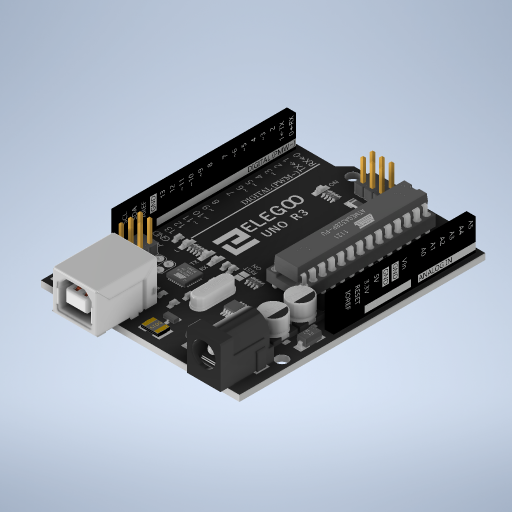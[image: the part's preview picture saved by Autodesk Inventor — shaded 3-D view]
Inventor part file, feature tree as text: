
AUTODESK INVENTOR PART (.ipt)
format: ipt  version: 2024 (Build 280153000, 153)  size: 18,806,272 bytes
history: native  units: in
note: dims shown in document units (in); Inventor stores cm internally (conversion verified against a paired STEP export)
features: other x713, projected_geometry x17, sketch x1
ambient origin geometry x8: Origin, YZ Plane, XZ Plane, XY Plane, X Axis, Y Axis, Z Axis, Center Point
bodies: Solid1 (feature_tree), Solid2 (feature_tree), Solid3 (feature_tree), Solid4 (feature_tree), Solid5 (feature_tree), Solid6 (feature_tree), Solid7 (feature_tree), Solid8 (feature_tree), Solid9 (feature_tree), Solid10 (feature_tree), Solid11 (feature_tree), Solid12 (feature_tree), Solid13 (feature_tree), Solid14 (feature_tree), Solid15 (feature_tree), Solid16 (feature_tree), Solid17 (feature_tree), Solid18 (feature_tree), Solid19 (feature_tree), Solid20 (feature_tree), Solid21 (feature_tree), Solid22 (feature_tree), Solid23 (feature_tree), Solid24 (feature_tree), Solid25 (feature_tree), Solid26 (feature_tree), Solid27 (feature_tree), Solid28 (feature_tree), Solid29 (feature_tree), Solid30 (feature_tree), Solid31 (feature_tree), Solid32 (feature_tree), Solid33 (feature_tree), Solid34 (feature_tree), Solid35 (feature_tree), Solid36 (feature_tree), Solid37 (feature_tree), Solid38 (feature_tree), Solid39 (feature_tree), Solid40 (feature_tree), Solid41 (feature_tree), Solid42 (feature_tree), Solid43 (feature_tree), Solid44 (feature_tree), Solid45 (feature_tree), Solid46 (feature_tree), Solid47 (feature_tree), Solid48 (feature_tree), Solid49 (feature_tree), Solid50 (feature_tree), Solid51 (feature_tree), Solid52 (feature_tree), Solid53 (feature_tree), Solid54 (feature_tree), Solid55 (feature_tree), Solid56 (feature_tree), Solid57 (feature_tree), Solid58 (feature_tree), Solid59 (feature_tree), Solid60 (feature_tree), Solid61 (feature_tree), Solid62 (feature_tree), Solid63 (feature_tree), Solid64 (feature_tree), Solid65 (feature_tree), Solid66 (feature_tree), Solid67 (feature_tree), Solid68 (feature_tree), Solid69 (feature_tree), Solid70 (feature_tree), Solid71 (feature_tree), Solid72 (feature_tree), Solid73 (feature_tree), Solid74 (feature_tree), Solid75 (feature_tree), Solid76 (feature_tree), Solid77 (feature_tree), Solid78 (feature_tree), Solid79 (feature_tree), Solid80 (feature_tree), Solid81 (feature_tree), Solid82 (feature_tree), Solid83 (feature_tree), Solid84 (feature_tree), Solid85 (feature_tree), Solid86 (feature_tree), Solid87 (feature_tree), Solid88 (feature_tree), Solid89 (feature_tree), Solid90 (feature_tree), Solid91 (feature_tree), Solid92 (feature_tree), Solid93 (feature_tree), Solid94 (feature_tree), Solid95 (feature_tree), Solid96 (feature_tree), Solid97 (feature_tree), Solid98 (feature_tree), Solid99 (feature_tree), Solid100 (feature_tree), Solid101 (feature_tree), Solid102 (feature_tree), Solid103 (feature_tree), Solid104 (feature_tree), Solid105 (feature_tree), Solid106 (feature_tree), Solid107 (feature_tree), Solid108 (feature_tree), Solid109 (feature_tree), Solid110 (feature_tree), Solid111 (feature_tree), Solid112 (feature_tree), Solid113 (feature_tree), Solid114 (feature_tree), Solid115 (feature_tree), Solid116 (feature_tree), Solid117 (feature_tree), Solid118 (feature_tree), Solid119 (feature_tree), Solid120 (feature_tree), Solid121 (feature_tree), Solid122 (feature_tree), Solid123 (feature_tree), Solid124 (feature_tree), Solid125 (feature_tree), Solid126 (feature_tree), Solid127 (feature_tree), Solid128 (feature_tree), Solid129 (feature_tree), Solid130 (feature_tree), Solid131 (feature_tree), Solid132 (feature_tree), Solid133 (feature_tree), Solid134 (feature_tree), Solid135 (feature_tree), Solid136 (feature_tree), Solid137 (feature_tree), Solid138 (feature_tree), Solid139 (feature_tree), Solid140 (feature_tree), Solid141 (feature_tree), Solid142 (feature_tree), Solid143 (feature_tree), Solid144 (feature_tree), Solid145 (feature_tree), Solid146 (feature_tree), Solid147 (feature_tree), Solid148 (feature_tree), Solid149 (feature_tree), Solid150 (feature_tree), Solid151 (feature_tree), Solid152 (feature_tree), Solid153 (feature_tree), Solid154 (feature_tree), Solid155 (feature_tree), Solid156 (feature_tree), Solid157 (feature_tree), Solid158 (feature_tree), Solid159 (feature_tree), Solid160 (feature_tree), Solid161 (feature_tree), Solid162 (feature_tree), Solid163 (feature_tree), Solid164 (feature_tree), Solid165 (feature_tree), Solid166 (feature_tree), Solid167 (feature_tree), Solid168 (feature_tree), Solid169 (feature_tree), Solid170 (feature_tree), Solid171 (feature_tree), Solid172 (feature_tree), Solid173 (feature_tree), Solid174 (feature_tree), Solid175 (feature_tree), Solid176 (feature_tree), Solid177 (feature_tree), Solid178 (feature_tree), Solid179 (feature_tree), Solid180 (feature_tree), Solid181 (feature_tree), Solid182 (feature_tree), Solid183 (feature_tree), Solid184 (feature_tree), Solid185 (feature_tree), Solid186 (feature_tree), Solid187 (feature_tree), Solid188 (feature_tree), Solid189 (feature_tree), Solid190 (feature_tree), Solid191 (feature_tree), Solid192 (feature_tree), Solid193 (feature_tree), Solid194 (feature_tree), Solid195 (feature_tree), Solid196 (feature_tree), Solid197 (feature_tree), Solid198 (feature_tree), Solid199 (feature_tree), Solid200 (feature_tree), Solid201 (feature_tree), Solid202 (feature_tree), Solid203 (feature_tree), Solid204 (feature_tree), Solid205 (feature_tree), Solid206 (feature_tree), Solid207 (feature_tree), Solid208 (feature_tree), Solid209 (feature_tree), Solid210 (feature_tree), Solid211 (feature_tree), Solid212 (feature_tree), Solid213 (feature_tree), Solid214 (feature_tree), Solid215 (feature_tree), Solid216 (feature_tree), Solid217 (feature_tree), Solid218 (feature_tree), Solid219 (feature_tree), Solid220 (feature_tree), Solid221 (feature_tree), Solid222 (feature_tree), Solid223 (feature_tree), Solid224 (feature_tree), Solid225 (feature_tree), Solid226 (feature_tree), Solid227 (feature_tree), Solid228 (feature_tree), Solid229 (feature_tree), Solid230 (feature_tree), Solid231 (feature_tree), Solid232 (feature_tree), Solid233 (feature_tree), Solid234 (feature_tree), Solid235 (feature_tree), Solid236 (feature_tree), Solid237 (feature_tree), Solid238 (feature_tree), Solid239 (feature_tree), Solid240 (feature_tree), Solid241 (feature_tree), Solid242 (feature_tree), Solid243 (feature_tree), Solid244 (feature_tree), Solid245 (feature_tree), Solid246 (feature_tree), Solid247 (feature_tree), Solid248 (feature_tree), Solid249 (feature_tree), Solid250 (feature_tree), Solid251 (feature_tree), Solid252 (feature_tree), Solid253 (feature_tree), Solid254 (feature_tree), Solid255 (feature_tree), Solid256 (feature_tree), Solid257 (feature_tree), Solid258 (feature_tree), Solid259 (feature_tree), Solid260 (feature_tree), Solid261 (feature_tree), Solid262 (feature_tree), Solid263 (feature_tree), Solid264 (feature_tree), Solid265 (feature_tree), Solid266 (feature_tree), Solid267 (feature_tree), Solid268 (feature_tree), Solid269 (feature_tree), Solid270 (feature_tree), Solid271 (feature_tree), Solid272 (feature_tree), Solid273 (feature_tree), Solid274 (feature_tree), Solid275 (feature_tree), Solid276 (feature_tree), Solid277 (feature_tree), Solid278 (feature_tree), Solid279 (feature_tree), Solid280 (feature_tree), Solid281 (feature_tree), Solid282 (feature_tree), Solid283 (feature_tree), Solid284 (feature_tree), Solid285 (feature_tree), Solid286 (feature_tree), Solid287 (feature_tree), Solid288 (feature_tree), Solid289 (feature_tree), Solid290 (feature_tree), Solid291 (feature_tree), Solid292 (feature_tree), Solid293 (feature_tree), Solid294 (feature_tree), Solid295 (feature_tree), Solid296 (feature_tree), Solid297 (feature_tree), Solid298 (feature_tree), Solid299 (feature_tree), Solid300 (feature_tree), Solid301 (feature_tree), Solid302 (feature_tree), Solid303 (feature_tree), Solid304 (feature_tree), Solid305 (feature_tree), Solid306 (feature_tree), Solid307 (feature_tree), Solid308 (feature_tree), Solid309 (feature_tree), Solid310 (feature_tree), Solid311 (feature_tree), Solid312 (feature_tree), Solid313 (feature_tree), Solid314 (feature_tree), Solid315 (feature_tree), Solid316 (feature_tree), Solid317 (feature_tree), Solid318 (feature_tree), Solid319 (feature_tree), Solid320 (feature_tree), Solid321 (feature_tree), Solid322 (feature_tree), Solid323 (feature_tree), Solid324 (feature_tree), Solid325 (feature_tree), Solid326 (feature_tree), Solid327 (feature_tree), Solid328 (feature_tree), Solid329 (feature_tree), Solid330 (feature_tree), Solid331 (feature_tree), Solid332 (feature_tree), Solid333 (feature_tree), Solid334 (feature_tree), Solid335 (feature_tree), Solid336 (feature_tree), Solid337 (feature_tree), Solid338 (feature_tree), Solid339 (feature_tree), Solid340 (feature_tree), Solid341 (feature_tree), Solid342 (feature_tree), Solid343 (feature_tree), Solid344 (feature_tree), Solid345 (feature_tree), Solid346 (feature_tree), Solid347 (feature_tree), Solid348 (feature_tree), Solid349 (feature_tree), Solid350 (feature_tree), Solid351 (feature_tree), Solid352 (feature_tree), Solid353 (feature_tree), Solid354 (feature_tree), Solid355 (feature_tree), Solid356 (feature_tree), Solid357 (feature_tree), Solid358 (feature_tree), Solid359 (feature_tree), Solid360 (feature_tree), Solid361 (feature_tree), Solid362 (feature_tree), Solid363 (feature_tree), Solid364 (feature_tree), Solid365 (feature_tree), Solid366 (feature_tree), Solid367 (feature_tree), Solid368 (feature_tree), Solid369 (feature_tree), Solid370 (feature_tree), Solid371 (feature_tree), Solid372 (feature_tree), Solid373 (feature_tree), Solid374 (feature_tree), Solid375 (feature_tree), Solid376 (feature_tree), Solid377 (feature_tree), Solid378 (feature_tree), Solid379 (feature_tree), Solid380 (feature_tree), Solid381 (feature_tree), Solid382 (feature_tree), Solid383 (feature_tree), Solid384 (feature_tree), Solid385 (feature_tree), Solid386 (feature_tree), Solid387 (feature_tree), Solid388 (feature_tree), Solid389 (feature_tree), Solid390 (feature_tree), Solid391 (feature_tree), Solid392 (feature_tree), Solid393 (feature_tree), Solid394 (feature_tree), Solid395 (feature_tree), Solid396 (feature_tree), Solid397 (feature_tree), Solid398 (feature_tree), Solid399 (feature_tree), Solid400 (feature_tree), Solid401 (feature_tree), Solid402 (feature_tree), Solid403 (feature_tree), Solid404 (feature_tree), Solid405 (feature_tree), Solid406 (feature_tree), Solid407 (feature_tree), Solid408 (feature_tree), Solid409 (feature_tree), Solid410 (feature_tree), Solid411 (feature_tree), Solid412 (feature_tree), Solid413 (feature_tree), Solid414 (feature_tree), Solid415 (feature_tree), Solid416 (feature_tree), Solid417 (feature_tree), Solid418 (feature_tree), Solid419 (feature_tree), Solid420 (feature_tree), Solid421 (feature_tree), Solid422 (feature_tree), Solid423 (feature_tree), Solid424 (feature_tree), Solid425 (feature_tree), Solid426 (feature_tree), Solid427 (feature_tree), Solid428 (feature_tree), Solid429 (feature_tree), Solid430 (feature_tree), Solid431 (feature_tree), Solid432 (feature_tree), Solid433 (feature_tree), Solid434 (feature_tree), Solid435 (feature_tree), Solid436 (feature_tree), Solid437 (feature_tree), Solid438 (feature_tree), Solid439 (feature_tree), Solid440 (feature_tree), Solid441 (feature_tree), Solid442 (feature_tree), Solid443 (feature_tree), Solid444 (feature_tree), Solid445 (feature_tree), Solid446 (feature_tree), Solid447 (feature_tree), Solid448 (feature_tree), Solid449 (feature_tree), Solid450 (feature_tree), Solid451 (feature_tree), Solid452 (feature_tree), Solid453 (feature_tree), Solid454 (feature_tree), Solid455 (feature_tree), Solid456 (feature_tree), Solid457 (feature_tree), Solid458 (feature_tree), Solid459 (feature_tree), Solid460 (feature_tree), Solid461 (feature_tree), Solid462 (feature_tree), Solid463 (feature_tree), Solid464 (feature_tree), Solid465 (feature_tree), Solid466 (feature_tree), Solid467 (feature_tree), Solid468 (feature_tree), Solid469 (feature_tree), Solid470 (feature_tree), Solid471 (feature_tree), Solid472 (feature_tree), Solid473 (feature_tree), Solid474 (feature_tree), Solid475 (feature_tree), Solid476 (feature_tree), Solid477 (feature_tree), Solid478 (feature_tree), Solid479 (feature_tree), Solid480 (feature_tree), Solid481 (feature_tree), Solid482 (feature_tree), Solid483 (feature_tree), Solid484 (feature_tree), Solid485 (feature_tree), Solid486 (feature_tree), Solid487 (feature_tree), Solid488 (feature_tree), Solid489 (feature_tree), Solid490 (feature_tree), Solid491 (feature_tree), Solid492 (feature_tree), Solid493 (feature_tree), Solid494 (feature_tree), Solid495 (feature_tree), Solid496 (feature_tree), Solid497 (feature_tree), Solid498 (feature_tree), Solid499 (feature_tree), Solid500 (feature_tree), Solid501 (feature_tree), Solid502 (feature_tree), Solid503 (feature_tree), Solid504 (feature_tree), Solid505 (feature_tree), Solid506 (feature_tree), Solid507 (feature_tree), Solid508 (feature_tree), Solid509 (feature_tree), Solid510 (feature_tree), Solid511 (feature_tree), Solid512 (feature_tree), Solid513 (feature_tree), Solid514 (feature_tree), Solid515 (feature_tree), Solid516 (feature_tree), Solid517 (feature_tree), Solid518 (feature_tree), Solid519 (feature_tree), Solid520 (feature_tree), Solid521 (feature_tree), Solid522 (feature_tree), Solid523 (feature_tree), Solid524 (feature_tree), Solid525 (feature_tree), Solid526 (feature_tree), Solid527 (feature_tree), Solid528 (feature_tree), Solid529 (feature_tree), Solid530 (feature_tree), Solid531 (feature_tree), Solid532 (feature_tree), Solid533 (feature_tree), Solid534 (feature_tree), Solid535 (feature_tree), Solid536 (feature_tree), Solid537 (feature_tree), Solid538 (feature_tree), Solid539 (feature_tree), Solid540 (feature_tree), Solid541 (feature_tree), Solid542 (feature_tree), Solid543 (feature_tree), Solid544 (feature_tree), Solid545 (feature_tree), Solid546 (feature_tree), Solid547 (feature_tree), Solid548 (feature_tree), Solid549 (feature_tree), Solid550 (feature_tree), Solid551 (feature_tree), Solid552 (feature_tree), Solid553 (feature_tree), Solid554 (feature_tree), Solid555 (feature_tree), Solid556 (feature_tree), Solid557 (feature_tree), Solid558 (feature_tree), Solid559 (feature_tree), Solid560 (feature_tree), Solid561 (feature_tree), Solid562 (feature_tree), Solid563 (feature_tree), Solid564 (feature_tree), Solid565 (feature_tree), Solid566 (feature_tree), Solid567 (feature_tree), Solid568 (feature_tree), Solid569 (feature_tree), Solid570 (feature_tree), Solid571 (feature_tree), Solid572 (feature_tree), Solid573 (feature_tree), Solid574 (feature_tree), Solid575 (feature_tree), Solid576 (feature_tree), Solid577 (feature_tree), Solid578 (feature_tree), Solid579 (feature_tree), Solid580 (feature_tree), Solid581 (feature_tree), Solid582 (feature_tree), Solid583 (feature_tree), Solid584 (feature_tree), Solid585 (feature_tree), Solid586 (feature_tree), Solid587 (feature_tree), Solid588 (feature_tree), Solid589 (feature_tree), Solid590 (feature_tree), Solid591 (feature_tree), Solid592 (feature_tree), Solid593 (feature_tree), Solid594 (feature_tree), Solid595 (feature_tree), Solid596 (feature_tree), Solid597 (feature_tree), Solid598 (feature_tree), Solid599 (feature_tree), Solid600 (feature_tree), Solid601 (feature_tree), Solid602 (feature_tree), Solid603 (feature_tree), Solid604 (feature_tree), Solid605 (feature_tree), Solid606 (feature_tree), Solid607 (feature_tree), Solid608 (feature_tree), Solid609 (feature_tree), Solid610 (feature_tree), Solid611 (feature_tree), Solid612 (feature_tree), Solid613 (feature_tree), Solid614 (feature_tree), Solid615 (feature_tree), Solid616 (feature_tree), Solid617 (feature_tree), Solid618 (feature_tree), Solid619 (feature_tree), Solid620 (feature_tree), Solid621 (feature_tree), Solid622 (feature_tree), Solid623 (feature_tree), Solid624 (feature_tree), Solid625 (feature_tree), Solid626 (feature_tree), Solid627 (feature_tree), Solid628 (feature_tree), Solid629 (feature_tree), Solid630 (feature_tree), Solid631 (feature_tree), Solid632 (feature_tree), Solid633 (feature_tree), Solid634 (feature_tree), Solid635 (feature_tree), Solid636 (feature_tree), Solid637 (feature_tree), Solid638 (feature_tree), Solid639 (feature_tree), Solid640 (feature_tree), Solid641 (feature_tree), Solid642 (feature_tree), Solid643 (feature_tree), Solid644 (feature_tree), Solid645 (feature_tree), Solid646 (feature_tree), Solid647 (feature_tree), Solid648 (feature_tree), Solid649 (feature_tree), Solid650 (feature_tree), Solid651 (feature_tree), Solid652 (feature_tree), Solid653 (feature_tree), Solid654 (feature_tree), Solid655 (feature_tree), Solid656 (feature_tree), Solid657 (feature_tree), Solid658 (feature_tree), Solid659 (feature_tree), Solid660 (feature_tree), Solid661 (feature_tree), Solid662 (feature_tree), Solid663 (feature_tree), Solid664 (feature_tree), Solid665 (feature_tree), Solid666 (feature_tree), Solid667 (feature_tree), Solid668 (feature_tree), Solid669 (feature_tree), Solid670 (feature_tree), Solid671 (feature_tree), Solid672 (feature_tree), Solid673 (feature_tree), Solid674 (feature_tree), Solid675 (feature_tree), Solid676 (feature_tree), Solid677 (feature_tree), Solid678 (feature_tree), Solid679 (feature_tree), Solid680 (feature_tree), Solid681 (feature_tree), Solid682 (feature_tree), Solid683 (feature_tree), Solid684 (feature_tree), Solid685 (feature_tree), Solid686 (feature_tree), Solid687 (feature_tree), Solid688 (feature_tree), Solid689 (feature_tree), Solid690 (feature_tree), Solid691 (feature_tree), Solid692 (feature_tree), Solid693 (feature_tree), Solid694 (feature_tree), Solid695 (feature_tree), Solid696 (feature_tree), Solid697 (feature_tree), Solid698 (feature_tree), Solid699 (feature_tree), Solid700 (feature_tree), Solid701 (feature_tree), Solid702 (feature_tree), Solid703 (feature_tree), Solid704 (feature_tree), Solid705 (feature_tree), Solid706 (feature_tree), Solid707 (feature_tree), Solid708 (feature_tree), Solid709 (feature_tree), Solid710 (feature_tree), Solid711 (feature_tree), Solid712 (feature_tree), Solid713 (feature_tree)
feature tree (731):
  sketch  "Sketch1"
  projected_geometry  "Projected Loop1"
  projected_geometry  "Projected Loop2"
  projected_geometry  "Projected Loop3"
  projected_geometry  "Projected Loop4"
  projected_geometry  "Projected Loop5"
  projected_geometry  "Projected Loop6"
  projected_geometry  "Projected Loop7"
  projected_geometry  "Projected Loop8"
  projected_geometry  "Projected Loop9"
  projected_geometry  "Projected Loop10"
  projected_geometry  "Projected Loop11"
  projected_geometry  "Projected Loop12"
  projected_geometry  "Projected Loop13"
  projected_geometry  "Projected Loop14"
  projected_geometry  "Projected Loop15"
  projected_geometry  "Projected Loop16"
  projected_geometry  "Projected Loop17"
  other  "I_O Headers"
  other  "I_O Headers:1"
  other  "I_O Headers:2"
  other  "I_O Headers:3"
  other  "I_O Headers:4"
  other  "I_O Headers:5"
  other  "I_O Headers:6"
  other  "I_O Headers:7"
  other  "I_O Headers:8"
  other  "I_O Headers:9"
  other  "I_O Headers:10"
  other  "I_O Headers:11"
  other  "I_O Headers:12"
  other  "I_O Headers:13"
  other  "I_O Headers:14"
  other  "I_O Headers:15"
  other  "I_O Headers:16"
  other  "I_O Headers:17"
  other  "I_O Headers:18"
  other  "I_O Headers:19"
  other  "I_O Headers:20"
  other  "I_O Headers:21"
  other  "I_O Headers:22"
  other  "I_O Headers:23"
  other  "I_O Headers:24"
  other  "I_O Headers:25"
  other  "I_O Headers:26"
  other  "I_O Headers:27"
  other  "I_O Headers:28"
  other  "I_O Headers:29"
  other  "I_O Headers:30"
  other  "I_O Headers:31"
  other  "I_O Headers:32"
  other  "I_O Headers:33"
  other  "I_O Headers:34"
  other  "I_O Headers:35"
  other  "I_O Headers:36"
  other  "I_O Headers:37"
  other  "I_O Headers:38"
  other  "I_O Headers:39"
  other  "I_O Headers:40"
  other  "I_O Headers:41"
  other  "I_O Headers:42"
  other  "I_O Headers:43"
  other  "I_O Headers:44"
  other  "I_O Headers:45"
  other  "I_O Headers:46"
  other  "I_O Headers:47"
  other  "I_O Headers:48"
  other  "I_O Headers:49"
  other  "I_O Headers:50"
  other  "I_O Headers:51"
  other  "I_O Headers:52"
  other  "I_O Headers:53"
  other  "I_O Headers:54"
  other  "I_O Headers:55"
  other  "I_O Headers:56"
  other  "I_O Headers:57"
  other  "I_O Headers:58"
  other  "I_O Headers:59"
  other  "I_O Headers:60"
  other  "I_O Headers:61"
  other  "I_O Headers:62"
  other  "I_O Headers:63"
  other  "I_O Headers:64"
  other  "I_O Headers:65"
  other  "I_O Headers:66"
  other  "I_O Headers:67"
  other  "I_O Headers:68"
  other  "I_O Headers:69"
  other  "I_O Headers:70"
  other  "I_O Headers:71"
  other  "I_O Headers:72"
  other  "I_O Headers:73"
  other  "I_O Headers:74"
  other  "I_O Headers:75"
  other  "I_O Headers:76"
  other  "I_O Headers:77"
  other  "I_O Headers:78"
  other  "I_O Headers:79"
  other  "I_O Headers:80"
  other  "I_O Headers:81"
  other  "I_O Headers:82"
  other  "I_O Headers:83"
  other  "I_O Headers:84"
  other  "I_O Headers:85"
  other  "I_O Headers:86"
  other  "I_O Headers:87"
  other  "I_O Headers:88"
  other  "I_O Headers:89"
  other  "I_O Headers:90"
  other  "I_O Headers:91"
  other  "I_O Headers:92"
  other  "I_O Headers:93"
  other  "I_O Headers:94"
  other  "I_O Headers:95"
  other  "I_O Headers:96"
  other  "I_O Headers:97"
  other  "I_O Headers:98"
  other  "I_O Headers:99"
  other  "I_O Headers:100"
  other  "I_O Headers:101"
  other  "I_O Headers:102"
  other  "I_O Headers:103"
  other  "I_O Headers:104"
  other  "I_O Headers:105"
  other  "I_O Headers:106"
  other  "I_O Headers:107"
  other  "I_O Headers:108"
  other  "I_O Headers:109"
  other  "I_O Headers:110"
  other  "I_O Headers:111"
  other  "I_O Headers:112"
  other  "I_O Headers:113"
  other  "I_O Headers:114"
  other  "I_O Headers:115"
  other  "I_O Headers:116"
  other  "I_O Headers:117"
  other  "I_O Headers:118"
  other  "I_O Headers:119"
  other  "I_O Headers:120"
  other  "I_O Headers:121"
  other  "I_O Headers:122"
  other  "I_O Headers:123"
  other  "I_O Headers:124"
  other  "I_O Headers:125"
  other  "I_O Headers:126"
  other  "I_O Headers:127"
  other  "I_O Headers:128"
  other  "I_O Headers:129"
  other  "I_O Headers:130"
  other  "I_O Headers:131"
  other  "I_O Headers:132"
  other  "I_O Headers:133"
  other  "I_O Headers:134"
  other  "I_O Headers:135"
  other  "I_O Headers:136"
  other  "I_O Headers:137"
  other  "I_O Headers:138"
  other  "I_O Headers:139"
  other  "I_O Headers:140"
  other  "I_O Headers:141"
  other  "I_O Headers:142"
  other  "I_O Headers:143"
  other  "I_O Headers:144"
  other  "I_O Headers:145"
  other  "I_O Headers:146"
  other  "I_O Headers:147"
  other  "I_O Headers:148"
  other  "I_O Headers:149"
  other  "I_O Headers:150"
  other  "I_O Headers:151"
  other  "I_O Headers:152"
  other  "I_O Headers:153"
  other  "I_O Headers:154"
  other  "I_O Headers:155"
  other  "I_O Headers:156"
  other  "I_O Headers:157"
  other  "I_O Headers:158"
  other  "I_O Headers:159"
  other  "I_O Headers:160"
  other  "I_O Headers:161"
  other  "I_O Headers:162"
  other  "I_O Headers:163"
  other  "I_O Headers:164"
  other  "I_O Headers:165"
  other  "I_O Headers:166"
  other  "I_O Headers:167"
  other  "I_O Headers:168"
  other  "I_O Headers:169"
  other  "I_O Headers:170"
  other  "I_O Headers:171"
  other  "I_O Headers:172"
  other  "I_O Headers:173"
  other  "I_O Headers:174"
  other  "I_O Headers:175"
  other  "I_O Headers:176"
  other  "I_O Headers:177"
  other  "I_O Headers:178"
  other  "I_O Headers:179"
  other  "I_O Headers:180"
  other  "I_O Headers:181"
  other  "I_O Headers:182"
  other  "I_O Headers:183"
  other  "I_O Headers:184"
  other  "I_O Headers:185"
  other  "I_O Headers:186"
  other  "I_O Headers:187"
  other  "I_O Headers:188"
  other  "I_O Headers:189"
  other  "I_O Headers:190"
  other  "I_O Headers:191"
  other  "I_O Headers:192"
  other  "I_O Headers:193"
  other  "I_O Headers:194"
  other  "I_O Headers:195"
  other  "I_O Headers:196"
  other  "I_O Headers:197"
  other  "I_O Headers:198"
  other  "I_O Headers:199"
  other  "I_O Headers:200"
  other  "I_O Headers:201"
  other  "I_O Headers:202"
  other  "I_O Headers:203"
  other  "I_O Headers:204"
  other  "I_O Headers:205"
  other  "I_O Headers:206"
  other  "I_O Headers:207"
  other  "I_O Headers:208"
  other  "I_O Headers:209"
  other  "brep_211"
  other  "brep_212"
  other  "brep_213"
  other  "brep_214"
  other  "brep_215"
  other  "brep_216"
  other  "brep_217"
  other  "brep_218"
  other  "brep_219"
  other  "brep_220"
  other  "brep_221"
  other  "brep_222"
  other  "brep_223"
  other  "brep_224"
  other  "brep_225"
  other  "brep_226"
  other  "brep_227"
  other  "brep_228"
  other  "brep_229"
  other  "brep_230"
  other  "brep_231"
  other  "brep_232"
  other  "brep_233"
  other  "brep_234"
  other  "brep_235"
  other  "brep_236"
  other  "brep_237"
  other  "brep_238"
  other  "brep_239"
  other  "brep_240"
  other  "brep_241"
  other  "brep_242"
  other  "brep_243"
  other  "brep_244"
  other  "brep_245"
  other  "brep_246"
  other  "brep_247"
  other  "brep_248"
  other  "brep_249"
  other  "brep_250"
  other  "brep_251"
  other  "brep_252"
  other  "brep_253"
  other  "brep_254"
  other  "brep_255"
  other  "brep_256"
  other  "brep_257"
  other  "brep_258"
  other  "brep_259"
  other  "brep_260"
  other  "brep_261"
  other  "brep_262"
  other  "brep_263"
  other  "brep_264"
  other  "brep_265"
  other  "brep_266"
  other  "brep_267"
  other  "brep_268"
  other  "brep_269"
  other  "brep_270"
  other  "brep_271"
  other  "brep_272"
  other  "brep_273"
  other  "brep_274"
  other  "brep_275"
  other  "brep_276"
  other  "brep_277"
  other  "brep_278"
  other  "brep_279"
  other  "brep_280"
  other  "brep_281"
  other  "brep_282"
  other  "brep_283"
  other  "brep_284"
  other  "brep_285"
  other  "brep_286"
  other  "brep_287"
  other  "brep_288"
  other  "brep_289"
  other  "brep_290"
  other  "brep_291"
  other  "brep_292"
  other  "brep_293"
  other  "brep_294"
  other  "brep_295"
  other  "brep_296"
  other  "brep_297"
  other  "brep_298"
  other  "brep_299"
  other  "brep_300"
  other  "brep_301"
  other  "brep_302"
  other  "brep_303"
  other  "brep_304"
  other  "brep_305"
  other  "brep_306"
  other  "brep_307"
  other  "brep_308"
  other  "brep_309"
  other  "brep_310"
  other  "brep_311"
  other  "brep_312"
  other  "brep_313"
  other  "brep_314"
  other  "brep_315"
  other  "brep_316"
  other  "brep_317"
  other  "brep_318"
  other  "brep_319"
  other  "brep_320"
  other  "brep_321"
  other  "brep_322"
  other  "brep_323"
  other  "brep_324"
  other  "brep_325"
  other  "brep_326"
  other  "brep_327"
  other  "brep_328"
  other  "brep_329"
  other  "brep_330"
  other  "brep_331"
  other  "brep_332"
  other  "brep_333"
  other  "brep_334"
  other  "brep_335"
  other  "brep_336"
  other  "brep_337"
  other  "brep_338"
  other  "brep_339"
  other  "brep_340"
  other  "brep_341"
  other  "brep_342"
  other  "brep_343"
  other  "brep_344"
  other  "brep_345"
  other  "brep_346"
  other  "brep_347"
  other  "brep_348"
  other  "brep_349"
  other  "brep_350"
  other  "brep_351"
  other  "brep_352"
  other  "brep_353"
  other  "brep_354"
  other  "brep_355"
  other  "brep_356"
  other  "brep_357"
  other  "brep_358"
  other  "brep_359"
  other  "brep_360"
  other  "brep_361"
  other  "brep_362"
  other  "brep_363"
  other  "brep_364"
  other  "brep_365"
  other  "brep_366"
  other  "brep_367"
  other  "brep_368"
  other  "brep_369"
  other  "brep_370"
  other  "brep_371"
  other  "brep_372"
  other  "brep_373"
  other  "brep_374"
  other  "brep_375"
  other  "brep_376"
  other  "brep_377"
  other  "brep_378"
  other  "brep_379"
  other  "brep_380"
  other  "brep_381"
  other  "brep_382"
  other  "brep_383"
  other  "brep_384"
  other  "brep_385"
  other  "brep_386"
  other  "brep_387"
  other  "brep_388"
  other  "brep_389"
  other  "USB Interface Chip"
  other  "USB Interface Chip:1"
  other  "USB Interface Chip:2"
  other  "USB Interface Chip:3"
  other  "USB Interface Chip:4"
  other  "USB Interface Chip:5"
  other  "USB Interface Chip:6"
  other  "USB Interface Chip:7"
  other  "USB Interface Chip:8"
  other  "USB Interface Chip:9"
  other  "USB Interface Chip:10"
  other  "USB Interface Chip:11"
  other  "USB Interface Chip:12"
  other  "USB Interface Chip:13"
  other  "USB Interface Chip:14"
  other  "USB Interface Chip:15"
  other  "USB Interface Chip:16"
  other  "USB Interface Chip:17"
  other  "USB Interface Chip:18"
  other  "USB Interface Chip:19"
  other  "USB Interface Chip:20"
  other  "USB Interface Chip:21"
  other  "USB Interface Chip:22"
  other  "USB Interface Chip:23"
  other  "USB Interface Chip:24"
  other  "USB Interface Chip:25"
  other  "USB Interface Chip:26"
  other  "USB Interface Chip:27"
  other  "USB Interface Chip:28"
  other  "USB Interface Chip:29"
  other  "USB Interface Chip:30"
  other  "USB Interface Chip:31"
  other  "USB Interface Chip:32"
  other  "USB Interface Chip:33"
  other  "USB Interface Chip:34"
  other  "USB Interface Chip:35"
  other  "USB Interface Chip:36"
  other  "USB Interface Chip:37"
  other  "USB Interface Chip:38"
  other  "USB Interface Chip:39"
  other  "USB Interface Chip:40"
  other  "USB Interface Chip:41"
  other  "USB Interface Chip:42"
  other  "USB Interface Chip:43"
  other  "USB Interface Chip:44"
  other  "USB Interface Chip:45"
  other  "USB Interface Chip:46"
  other  "USB Interface Chip:47"
  other  "USB Interface Chip:48"
  other  "USB Interface Chip:49"
  other  "USB Interface Chip:50"
  other  "USB Interface Chip:51"
  other  "USB Interface Chip:52"
  other  "USB Interface Chip:53"
  other  "USB Interface Chip:54"
  other  "USB Interface Chip:55"
  other  "USB Interface Chip:56"
  other  "USB Interface Chip:57"
  other  "USB Interface Chip:58"
  other  "USB Interface Chip:59"
  other  "brep_450"
  other  "brep_451"
  other  "brep_452"
  other  "brep_453"
  other  "brep_454"
  other  "brep_455"
  other  "brep_456"
  other  "brep_457"
  other  "brep_458"
  other  "brep_459"
  other  "brep_460"
  other  "brep_461"
  other  "brep_462"
  other  "brep_463"
  other  "brep_464"
  other  "brep_465"
  other  "brep_466"
  other  "brep_467"
  other  "brep_468"
  other  "brep_469"
  other  "brep_470"
  other  "brep_471"
  other  "brep_472"
  other  "I_O Headers:210"
  other  "I_O Headers:211"
  other  "I_O Headers:212"
  other  "I_O Headers:213"
  other  "I_O Headers:214"
  other  "I_O Headers:215"
  other  "I_O Headers:216"
  other  "I_O Headers:217"
  other  "I_O Headers:218"
  other  "brep_482"
  other  "brep_483"
  other  "brep_484"
  other  "brep_485"
  other  "brep_486"
  other  "brep_487"
  other  "brep_488"
  other  "brep_489"
  other  "brep_490"
  other  "brep_491"
  other  "brep_492"
  other  "brep_493"
  other  "brep_494"
  other  "brep_495"
  other  "brep_496"
  other  "brep_497"
  other  "brep_498"
  other  "brep_499"
  other  "brep_500"
  other  "brep_501"
  other  "brep_502"
  other  "brep_503"
  other  "brep_504"
  other  "brep_505"
  other  "brep_506"
  other  "brep_507"
  other  "brep_508"
  other  "brep_509"
  other  "brep_510"
  other  "Pin 13 LED"
  other  "Pin 13 LED:1"
  other  "Pin 13 LED:2"
  other  "TX LED"
  other  "TX LED:1"
  other  "TX LED:2"
  other  "RX LED"
  other  "RX LED:1"
  other  "RX LED:2"
  other  "brep_520"
  other  "brep_521"
  other  "brep_522"
  other  "brep_523"
  other  "brep_524"
  other  "brep_525"
  other  "brep_526"
  other  "brep_527"
  other  "brep_528"
  other  "brep_529"
  other  "brep_530"
  other  "brep_531"
  other  "brep_532"
  other  "brep_533"
  other  "brep_534"
  other  "brep_535"
  other  "brep_536"
  other  "brep_537"
  other  "brep_538"
  other  "Power LED"
  other  "Power LED:1"
  other  "Power LED:2"
  other  "I_O Headers:219"
  other  "I_O Headers:220"
  other  "I_O Headers:221"
  other  "I_O Headers:222"
  other  "I_O Headers:223"
  other  "I_O Headers:224"
  other  "I_O Headers:225"
  other  "I_O Headers:226"
  other  "I_O Headers:227"
  other  "Atmega 328P Microcontroller"
  other  "Atmega 328P Microcontroller:1"
  other  "Atmega 328P Microcontroller:2"
  other  "Atmega 328P Microcontroller:3"
  other  "Atmega 328P Microcontroller:4"
  other  "Atmega 328P Microcontroller:5"
  other  "Atmega 328P Microcontroller:6"
  other  "Atmega 328P Microcontroller:7"
  other  "Atmega 328P Microcontroller:8"
  other  "Atmega 328P Microcontroller:9"
  other  "Atmega 328P Microcontroller:10"
  other  "Atmega 328P Microcontroller:11"
  other  "Atmega 328P Microcontroller:12"
  other  "Atmega 328P Microcontroller:13"
  other  "Atmega 328P Microcontroller:14"
  other  "Atmega 328P Microcontroller:15"
  other  "Atmega 328P Microcontroller:16"
  other  "Atmega 328P Microcontroller:17"
  other  "Atmega 328P Microcontroller:18"
  other  "Atmega 328P Microcontroller:19"
  other  "Atmega 328P Microcontroller:20"
  other  "Atmega 328P Microcontroller:21"
  other  "Atmega 328P Microcontroller:22"
  other  "Atmega 328P Microcontroller:23"
  other  "Atmega 328P Microcontroller:24"
  other  "Atmega 328P Microcontroller:25"
  other  "Atmega 328P Microcontroller:26"
  other  "Atmega 328P Microcontroller:27"
  other  "I_O Headers:228"
  other  "I_O Headers:229"
  other  "I_O Headers:230"
  other  "I_O Headers:231"
  other  "I_O Headers:232"
  other  "I_O Headers:233"
  other  "I_O Headers:234"
  other  "I_O Headers:235"
  other  "I_O Headers:236"
  other  "I_O Headers:237"
  other  "I_O Headers:238"
  other  "I_O Headers:239"
  other  "I_O Headers:240"
  other  "I_O Headers:241"
  other  "brep_593"
  other  "brep_594"
  other  "brep_595"
  other  "brep_596"
  other  "brep_597"
  other  "brep_598"
  other  "brep_599"
  other  "brep_600"
  other  "brep_601"
  other  "brep_602"
  other  "brep_603"
  other  "brep_604"
  other  "brep_605"
  other  "brep_606"
  other  "brep_607"
  other  "brep_608"
  other  "brep_609"
  other  "brep_610"
  other  "brep_611"
  other  "brep_612"
  other  "brep_613"
  other  "5.5mm DC Barrel Jack"
  other  "5.5mm DC Barrel Jack:1"
  other  "5.5mm DC Barrel Jack:2"
  other  "5.5mm DC Barrel Jack:3"
  other  "5.5mm DC Barrel Jack:4"
  other  "Voltage Regulator"
  other  "Voltage Regulator:1"
  other  "Voltage Regulator:2"
  other  "Voltage Regulator:3"
  other  "Voltage Regulator:4"
  other  "brep_624"
  other  "brep_625"
  other  "brep_626"
  other  "brep_627"
  other  "brep_628"
  other  "brep_629"
  other  "brep_630"
  other  "Reset Button"
  other  "Reset Button:1"
  other  "brep_633"
  other  "brep_634"
  other  "brep_635"
  other  "brep_636"
  other  "brep_637"
  other  "brep_638"
  other  "brep_639"
  other  "brep_640"
  other  "brep_641"
  other  "brep_642"
  other  "brep_643"
  other  "brep_644"
  other  "brep_645"
  other  "brep_646"
  other  "brep_647"
  other  "brep_648"
  other  "brep_649"
  other  "brep_650"
  other  "brep_651"
  other  "brep_652"
  other  "brep_653"
  other  "brep_654"
  other  "brep_655"
  other  "brep_656"
  other  "5.5mm DC Barrel Jack:5"
  other  "brep_658"
  other  "Crystal Oscillator"
  other  "Atmega 328P Microcontroller:28"
  other  "Atmega 328P Microcontroller:29"
  other  "Atmega 328P Microcontroller:30"
  other  "Atmega 328P Microcontroller:31"
  other  "Atmega 328P Microcontroller:32"
  other  "Atmega 328P Microcontroller:33"
  other  "Atmega 328P Microcontroller:34"
  other  "Atmega 328P Microcontroller:35"
  other  "Atmega 328P Microcontroller:36"
  other  "Atmega 328P Microcontroller:37"
  other  "brep_670"
  other  "brep_671"
  other  "brep_672"
  other  "brep_673"
  other  "brep_674"
  other  "brep_675"
  other  "brep_676"
  other  "brep_677"
  other  "brep_678"
  other  "USB"
  other  "USB:1"
  other  "USB:2"
  other  "USB:3"
  other  "USB:4"
  other  "USB:5"
  other  "brep_685"
  other  "brep_686"
  other  "brep_687"
  other  "brep_688"
  other  "brep_689"
  other  "brep_690"
  other  "brep_691"
  other  "brep_692"
  other  "brep_693"
  other  "brep_694"
  other  "brep_695"
  other  "brep_696"
  other  "brep_697"
  other  "brep_698"
  other  "brep_699"
  other  "brep_700"
  other  "brep_701"
  other  "brep_702"
  other  "brep_703"
  other  "brep_704"
  other  "brep_705"
  other  "brep_706"
  other  "brep_707"
  other  "brep_708"
  other  "brep_709"
  other  "brep_710"
  other  "brep_711"
  other  "brep_712"
  other  "brep_713"
